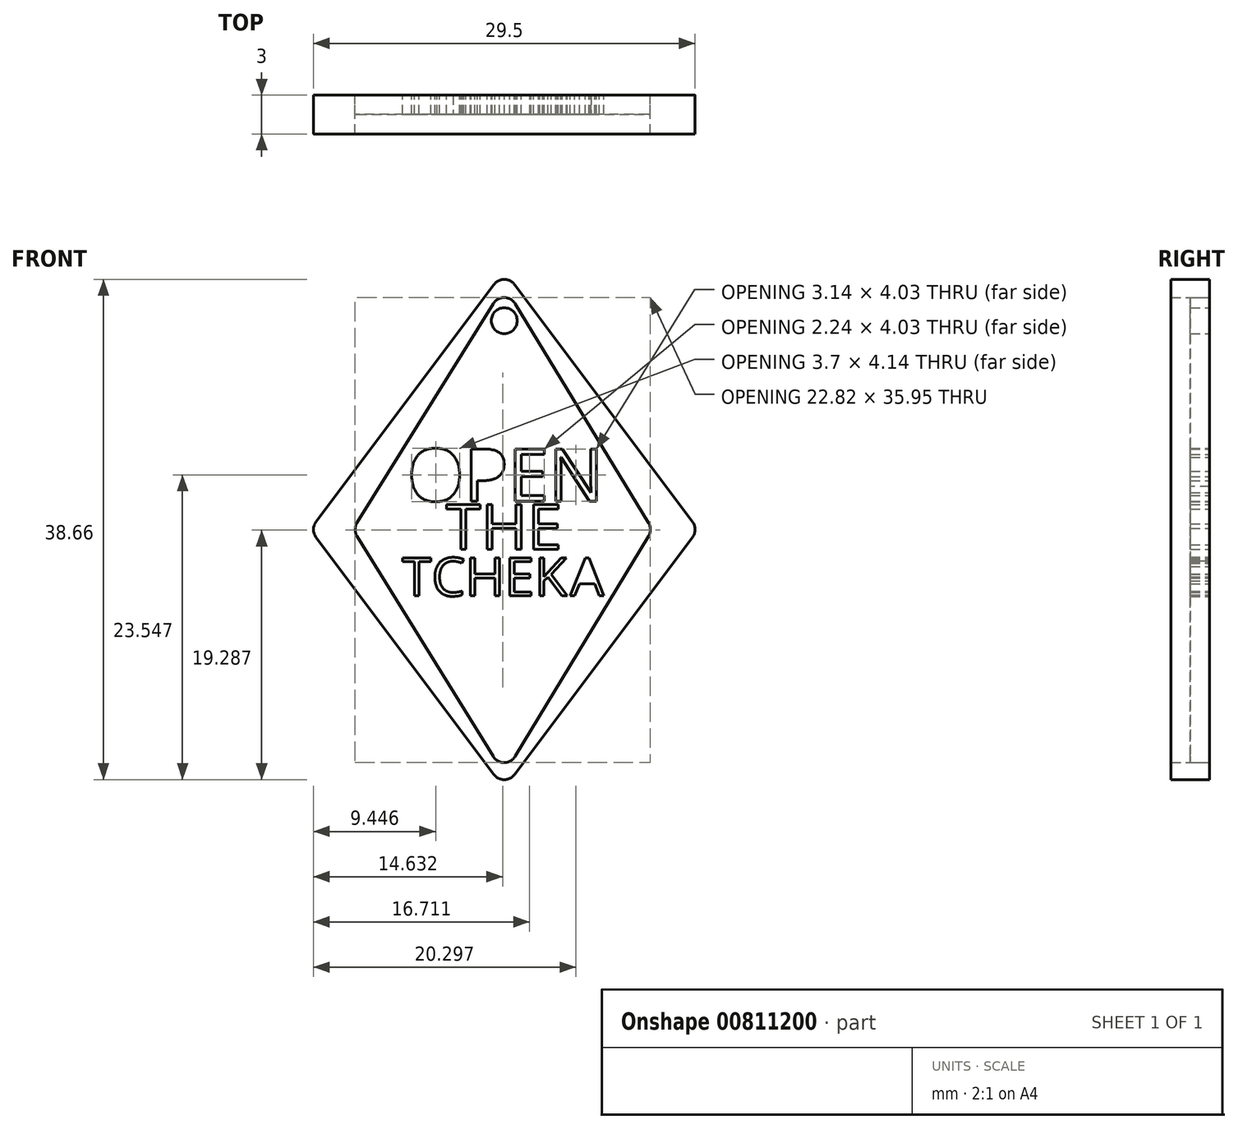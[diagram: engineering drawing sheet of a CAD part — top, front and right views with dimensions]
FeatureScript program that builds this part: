
annotation { "Feature Type Name" : "Feature", "Feature Type Description" : "" }
export const myFeature = defineFeature(function(context is Context, id is Id, definition is map)
    precondition{}
    {
        {
            var Q0;
            Q0=qCreatedBy(makeId("Front.planeOp"),FACE);
            var sketch = newSketch(context, id + "F0", { "sketchPlane" : qUnion([Q0])});
            skPoint(sketch, "E0.middle", {"position": v(0, 0) * mm});
            skLineSegment(sketch, "E1", {"start": v(-0.8, 18.93) * mm, "end": v(-14.55, 0.6) * mm});
            skLineSegment(sketch, "E2", {"start": v(-14.55, -0.6) * mm, "end": v(-0.8, -18.93) * mm});
            skLineSegment(sketch, "E3", {"start": v(0.8, -18.93) * mm, "end": v(14.55, -0.6) * mm});
            skLineSegment(sketch, "E4", {"start": v(14.55, 0.6) * mm, "end": v(0.8, 18.93) * mm});
            skPoint(sketch, "E5.visualSharp", {"position": v(-15, 0) * mm});
            skArc(sketch, "E5.filletArc", {"start": v(-14.55, 0.6) * mm, "mid": v(-14.75, 0) * mm, "end": v(-14.55, -0.6) * mm});
            skPoint(sketch, "E6.visualSharp", {"position": v(15, 0) * mm});
            skArc(sketch, "E6.filletArc", {"start": v(14.55, -0.6) * mm, "mid": v(14.75, 0) * mm, "end": v(14.55, 0.6) * mm});
            skArc(sketch, "E7.filletArc", {"start": v(-0.8, -18.93) * mm, "mid": v(0, -19.33) * mm, "end": v(0.8, -18.93) * mm});
            skArc(sketch, "E8.filletArc", {"start": v(0.8, 18.93) * mm, "mid": v(0, 19.33) * mm, "end": v(-0.8, 18.93) * mm});
            skLineSegment(sketch, "E9", {"start": v(11.15, 0.52) * mm, "end": v(0.85, 17.45) * mm});
            skLineSegment(sketch, "E10", {"start": v(-0.86, 17.46) * mm, "end": v(-11.38, 0.53) * mm});
            skLineSegment(sketch, "E11", {"start": v(-11.38, -0.53) * mm, "end": v(-0.86, -17.54) * mm});
            skLineSegment(sketch, "E12", {"start": v(0.85, -17.54) * mm, "end": v(11.15, -0.52) * mm});
            skText(sketch, "E13", { "text": "OPEN", "fontName": "OpenSans-Regular.ttf"});
            skText(sketch, "E14", { "text": "THE", "fontName": "OpenSans-Regular.ttf"});
            skCircle(sketch, "E15", {"center": v(0, 16.14) * mm, "radius": 1 * mm});
            skPoint(sketch, "E16.visualSharp", {"position": v(0, -18.93) * mm});
            skArc(sketch, "E16.filletArc", {"start": v(-0.86, -17.54) * mm, "mid": v(0, -18.02) * mm, "end": v(0.85, -17.54) * mm});
            skPoint(sketch, "E17.visualSharp", {"position": v(0, 18.84) * mm});
            skArc(sketch, "E17.filletArc", {"start": v(0.85, 17.45) * mm, "mid": v(0, 17.93) * mm, "end": v(-0.86, 17.46) * mm});
            skPoint(sketch, "E18.visualSharp", {"position": v(11.46, 0) * mm});
            skArc(sketch, "E18.filletArc", {"start": v(11.15, -0.52) * mm, "mid": v(11.3, 0) * mm, "end": v(11.15, 0.52) * mm});
            skPoint(sketch, "E19.visualSharp", {"position": v(-11.7, 0) * mm});
            skArc(sketch, "E19.filletArc", {"start": v(-11.38, 0.53) * mm, "mid": v(-11.53, 0) * mm, "end": v(-11.38, -0.53) * mm});
            skText(sketch, "E20", { "text": "TCHEK", "fontName": "OpenSans-Regular.ttf"});
            skText(sketch, "E21", { "text": "A", "fontName": "OpenSans-Regular.ttf"});
            const initialGuessF0  = {"E13": [-0.0075, 0.0022, 1, 0, 0.00406], "E14": [-0.0045, -0.00154, 1, 0, 0.0035], "E20": [-0.0079, -0.00513, 1, 0, 0.00297], "E21": [0.0051, -0.00513, 1, 0, 0.00296]};
            skSetInitialGuess(sketch, initialGuessF0);
            skSolve(sketch);
        }
        {
            var Q0;
            Q0=makeQuery(id+"F0.imprint","IMPRINT",FACE,{"disambiguationData":[TD([[makeQuery(id+"F0.imprint","IMPRINT",EDGE,{"derivedFrom":sQuery(id+"F0.wireOp",EDGE,"E1")}),1.0]])]});
            extrude(context, id + "F1", {"entities" : qUnion([Q0]), "depth" : 3 * mm, "offsetDistance" : 25 * mm});
        }
        {
            var Q0;
            Q0=makeQuery(id+"F0.imprint","IMPRINT",FACE,{"disambiguationData":[TD([[makeQuery(id+"F0.imprint","IMPRINT",EDGE,{"derivedFrom":sQuery(id+"F0.wireOp",EDGE,"E9")}),1.0]])]});
            extrude(context, id + "F2", {"entities" : qUnion([Q0]), "depth" : 1.5 * mm, "offsetDistance" : 25 * mm});
        }
    });
